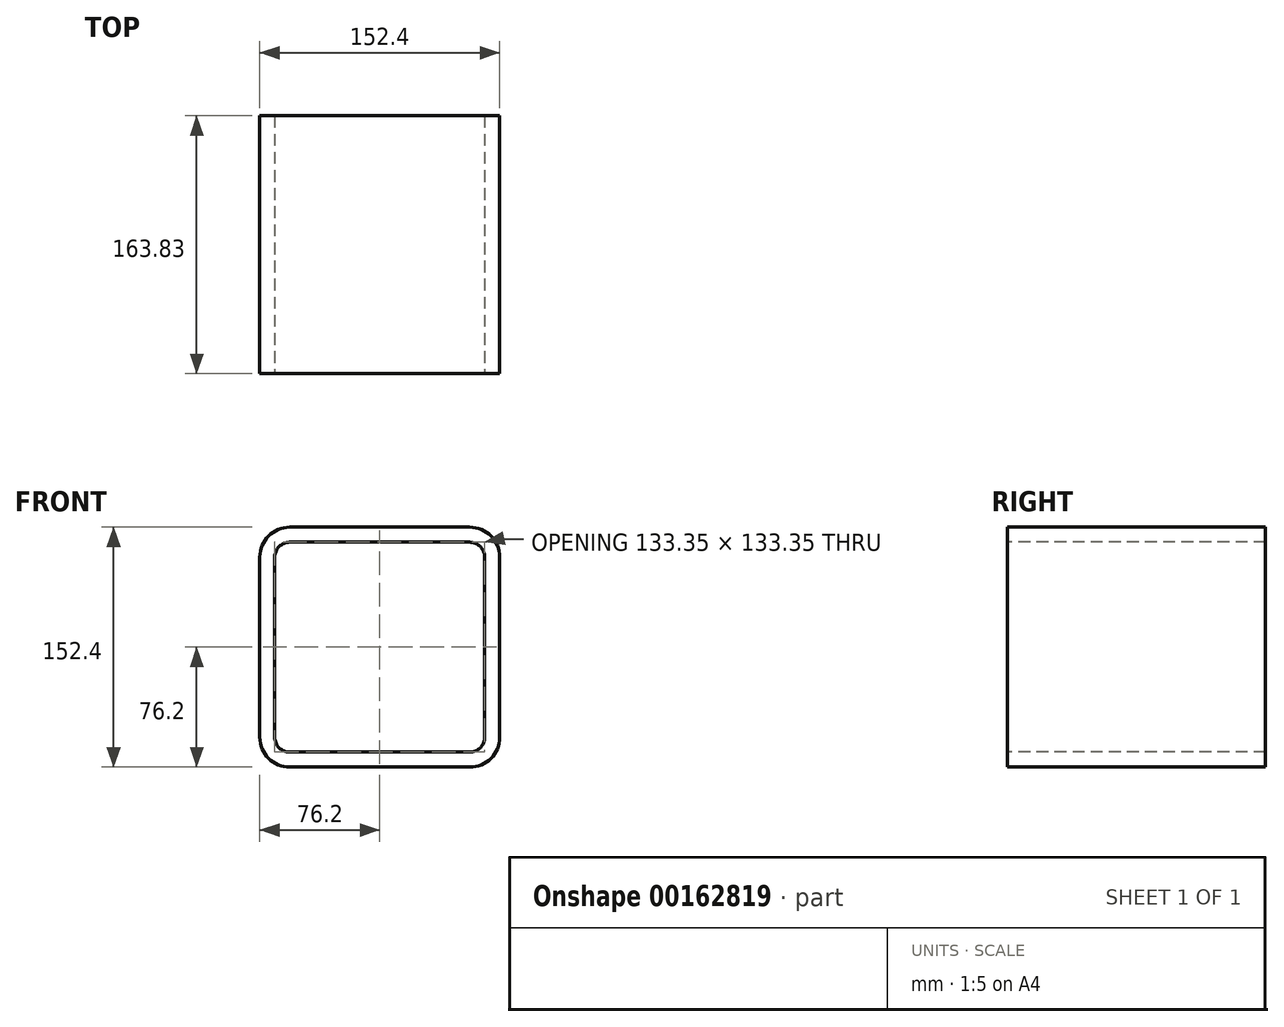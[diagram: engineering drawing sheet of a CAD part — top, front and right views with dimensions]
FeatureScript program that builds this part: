
annotation { "Feature Type Name" : "Feature", "Feature Type Description" : "" }
export const myFeature = defineFeature(function(context is Context, id is Id, definition is map)
    precondition{}
    {
        {
            var Q0;
            Q0=qCreatedBy(makeId("Front.planeOp"),FACE);
            var sketch = newSketch(context, id + "F0", { "sketchPlane" : qUnion([Q0])});
            skLineSegment(sketch, "E0.bottom", {"start": v(-57.15, 76.2) * mm, "end": v(57.15, 76.2) * mm});
            skLineSegment(sketch, "E0.top", {"start": v(-57.15, -76.2) * mm, "end": v(57.15, -76.2) * mm});
            skLineSegment(sketch, "E0.left", {"start": v(-76.2, 57.15) * mm, "end": v(-76.2, -57.15) * mm});
            skLineSegment(sketch, "E0.right", {"start": v(76.2, 57.15) * mm, "end": v(76.2, -57.15) * mm});
            skLineSegment(sketch, "E1", {"start": v(-76.2, 76.2) * mm, "end": v(76.2, -76.2) * mm, "construction": true});
            skPoint(sketch, "E2.visualSharp", {"position": v(-76.2, 76.2) * mm});
            skArc(sketch, "E2.filletArc", {"start": v(-57.15, 76.2) * mm, "mid": v(-70.62, 70.62) * mm, "end": v(-76.2, 57.15) * mm});
            skPoint(sketch, "E3.visualSharp", {"position": v(-76.2, -76.2) * mm});
            skArc(sketch, "E3.filletArc", {"start": v(-76.2, -57.15) * mm, "mid": v(-70.62, -70.62) * mm, "end": v(-57.15, -76.2) * mm});
            skPoint(sketch, "E4.visualSharp", {"position": v(76.2, -76.2) * mm});
            skArc(sketch, "E4.filletArc", {"start": v(57.15, -76.2) * mm, "mid": v(70.62, -70.62) * mm, "end": v(76.2, -57.15) * mm});
            skPoint(sketch, "E5.visualSharp", {"position": v(76.2, 76.2) * mm});
            skArc(sketch, "E5.filletArc", {"start": v(76.2, 57.15) * mm, "mid": v(70.62, 70.62) * mm, "end": v(57.15, 76.2) * mm});
            skLineSegment(sketch, "E6.0", {"start": v(-57.15, 66.68) * mm, "end": v(57.15, 66.68) * mm});
            skArc(sketch, "E7.0", {"start": v(-57.15, 66.68) * mm, "mid": v(-63.89, 63.89) * mm, "end": v(-66.68, 57.15) * mm});
            skLineSegment(sketch, "E8.0", {"start": v(-66.67, 57.15) * mm, "end": v(-66.68, -57.15) * mm});
            skArc(sketch, "E9.0", {"start": v(66.68, 57.15) * mm, "mid": v(63.89, 63.89) * mm, "end": v(57.15, 66.68) * mm});
            skLineSegment(sketch, "E10.0", {"start": v(66.68, 57.15) * mm, "end": v(66.67, -57.15) * mm});
            skLineSegment(sketch, "E11.0", {"start": v(-57.15, -66.67) * mm, "end": v(57.15, -66.67) * mm});
            skArc(sketch, "E12.0", {"start": v(-66.68, -57.15) * mm, "mid": v(-63.89, -63.89) * mm, "end": v(-57.15, -66.68) * mm});
            skArc(sketch, "E13.0", {"start": v(57.15, -66.67) * mm, "mid": v(63.89, -63.89) * mm, "end": v(66.67, -57.15) * mm});
            skSolve(sketch);
        }
        {
            var Q0;
            Q0=makeQuery(id+"F0.imprint","IMPRINT",FACE,{"disambiguationData":[TD([[makeQuery(id+"F0.imprint","IMPRINT",EDGE,{"derivedFrom":sQuery(id+"F0.wireOp",EDGE,"E0.bottom")}),-1.0]])]});
            extrude(context, id + "F1", {"entities" : qUnion([Q0]), "oppositeDirection" : true, "depth" : 163.83 * mm});
        }
    });
